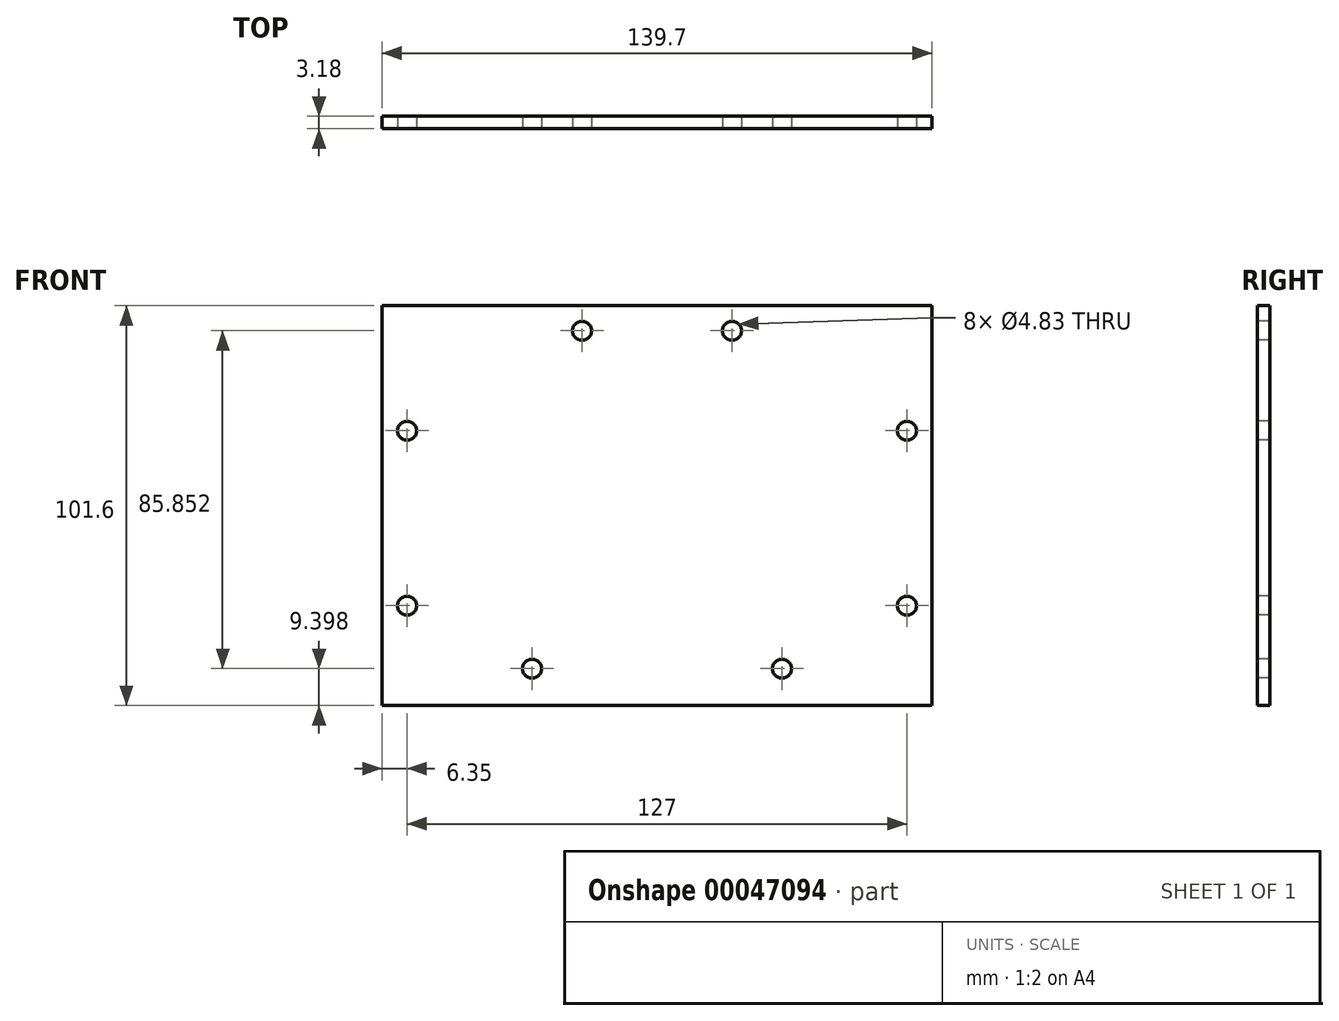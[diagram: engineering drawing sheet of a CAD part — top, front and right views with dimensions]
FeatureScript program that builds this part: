
annotation { "Feature Type Name" : "Feature", "Feature Type Description" : "" }
export const myFeature = defineFeature(function(context is Context, id is Id, definition is map)
    precondition{}
    {
        {
            var Q0;
            Q0=qCreatedBy(makeId("Front.planeOp"),FACE);
            var sketch = newSketch(context, id + "F0", { "sketchPlane" : qUnion([Q0])});
            skLineSegment(sketch, "E0.rect.bottom", {"start": v(69.85, 50.8) * mm, "end": v(-69.85, 50.8) * mm});
            skLineSegment(sketch, "E0.rect.top", {"start": v(69.85, -50.8) * mm, "end": v(-69.85, -50.8) * mm});
            skLineSegment(sketch, "E0.rect.left", {"start": v(69.85, 50.8) * mm, "end": v(69.85, -50.8) * mm});
            skLineSegment(sketch, "E0.rect.right", {"start": v(-69.85, 50.8) * mm, "end": v(-69.85, -50.8) * mm});
            skPoint(sketch, "E0.rect.middle", {"position": v(0, 0) * mm});
            skSolve(sketch);
        }
        {
            var Q0;
            Q0 = qSketchRegion(id + "F0", true);
            extrude(context, id + "F1", {"entities" : qUnion([Q0]), "endBound" : BoundingType.SYMMETRIC, "depth" : 3.17 * mm});
        }
        {
            var Q0;
            Q0=qCreatedBy(makeId("Front.planeOp"),FACE);
            var sketch = newSketch(context, id + "F2", { "sketchPlane" : qUnion([Q0])});
            skCircle(sketch, "E1", {"center": v(19.05, 44.45) * mm, "radius": 2.41 * mm});
            skCircle(sketch, "E2", {"center": v(-19.05, 44.45) * mm, "radius": 2.41 * mm});
            skCircle(sketch, "E3", {"center": v(-63.5, 19.05) * mm, "radius": 2.41 * mm});
            skCircle(sketch, "E4", {"center": v(-63.5, -25.4) * mm, "radius": 2.41 * mm});
            skCircle(sketch, "E5", {"center": v(63.5, 19.05) * mm, "radius": 2.41 * mm});
            skCircle(sketch, "E6", {"center": v(63.5, -25.4) * mm, "radius": 2.41 * mm});
            skCircle(sketch, "E7", {"center": v(-31.75, -41.4) * mm, "radius": 2.41 * mm});
            skCircle(sketch, "E8", {"center": v(31.75, -41.4) * mm, "radius": 2.41 * mm});
            skSolve(sketch);
        }
        {
            var Q0;
            Q0 = qSketchRegion(id + "F2", true);
            extrude(context, id + "F3", {"entities" : qUnion([Q0]), "operationType" : NewBodyOperationType.REMOVE, "endBound" : BoundingType.SYMMETRIC, "oppositeDirection" : true, "depth" : 3.17 * mm});
        }
    });
